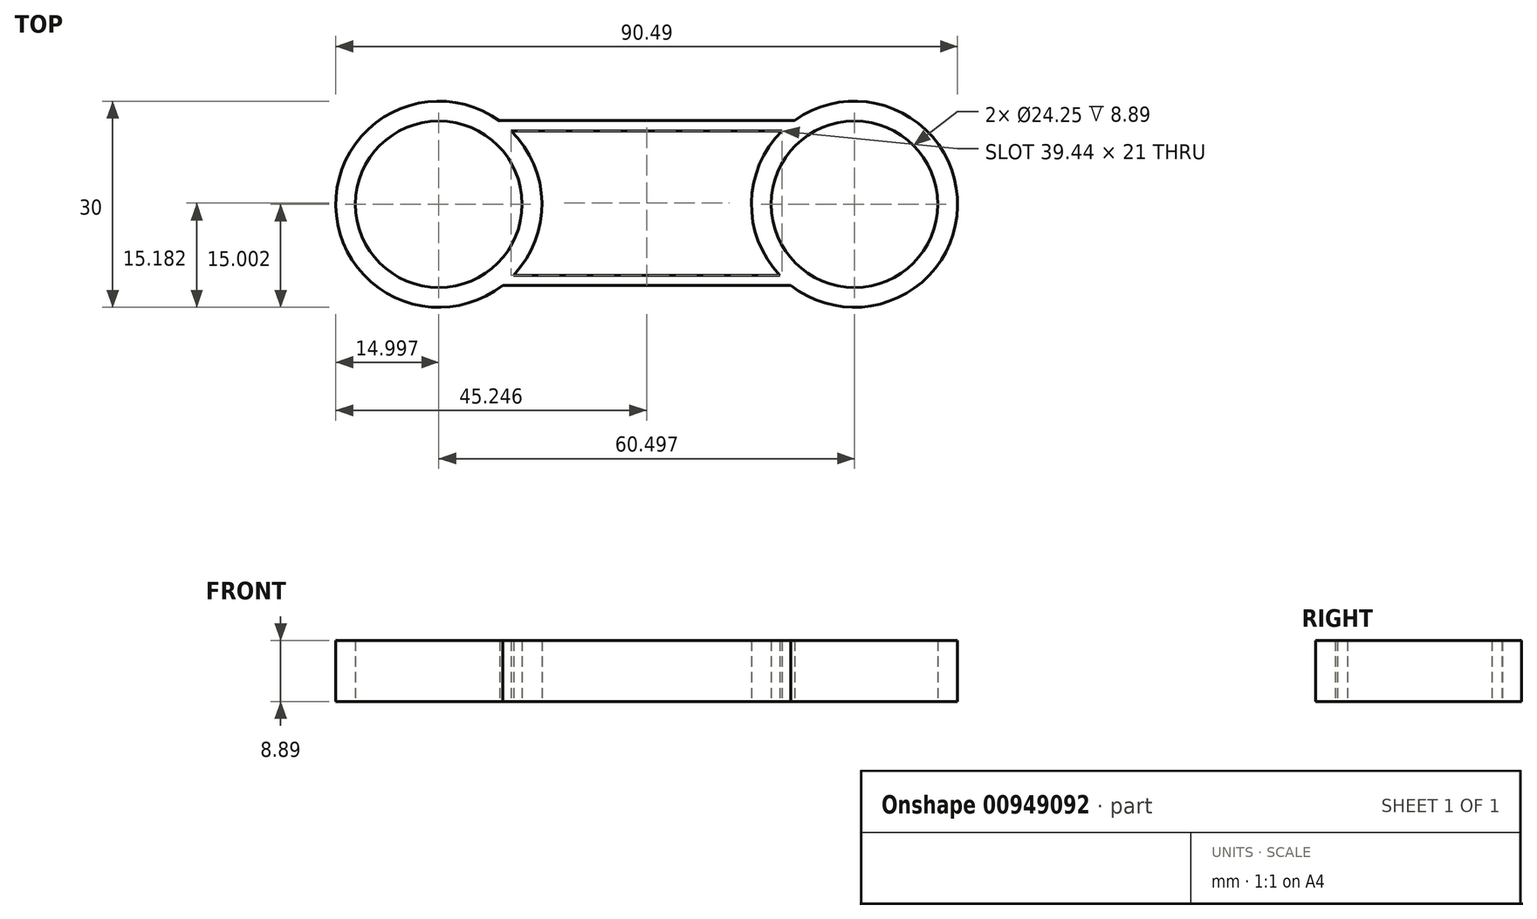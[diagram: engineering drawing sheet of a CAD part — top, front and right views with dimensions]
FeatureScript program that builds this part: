
annotation { "Feature Type Name" : "Feature", "Feature Type Description" : "" }
export const myFeature = defineFeature(function(context is Context, id is Id, definition is map)
    precondition{}
    {
        {
            var Q0;
            Q0=qCreatedBy(makeId("Top.planeOp"),FACE);
            var sketch = newSketch(context, id + "F0", { "sketchPlane" : qUnion([Q0])});
            skLineSegment(sketch, "E0.bottom", {"start": v(-19.42, -11.2) * mm, "end": v(23.58, -11.2) * mm});
            skLineSegment(sketch, "E0.top", {"start": v(-19.42, 12.8) * mm, "end": v(23.58, 12.8) * mm});
            skLineSegment(sketch, "E0.left", {"start": v(-19.42, -11.2) * mm, "end": v(-19.42, 12.8) * mm});
            skLineSegment(sketch, "E0.right", {"start": v(23.58, -11.2) * mm, "end": v(23.58, 12.8) * mm});
            skLineSegment(sketch, "E1.bottom", {"start": v(-18.21, -9.74) * mm, "end": v(22.29, -9.74) * mm});
            skLineSegment(sketch, "E1.top", {"start": v(-18.21, 11.26) * mm, "end": v(22.29, 11.26) * mm});
            skLineSegment(sketch, "E1.left", {"start": v(-18.21, -9.74) * mm, "end": v(-18.21, 11.26) * mm});
            skLineSegment(sketch, "E1.right", {"start": v(22.29, -9.74) * mm, "end": v(22.29, 11.26) * mm});
            skCircle(sketch, "E2", {"center": v(-28.27, 0.58) * mm, "radius": 12.12 * mm});
            skCircle(sketch, "E3", {"center": v(-28.27, 0.58) * mm, "radius": 15 * mm});
            skCircle(sketch, "E4", {"center": v(32.22, 0.58) * mm, "radius": 15 * mm});
            skCircle(sketch, "E5", {"center": v(32.22, 0.58) * mm, "radius": 12.12 * mm});
            skLineSegment(sketch, "E6.bottom", {"start": v(-43.27, -14.42) * mm, "end": v(47.22, -14.42) * mm});
            skLineSegment(sketch, "E6.top", {"start": v(-43.27, 15.58) * mm, "end": v(47.22, 15.58) * mm});
            skLineSegment(sketch, "E6.left", {"start": v(-43.27, -14.42) * mm, "end": v(-43.27, 15.58) * mm});
            skLineSegment(sketch, "E6.right", {"start": v(47.22, -14.42) * mm, "end": v(47.22, 15.58) * mm});
            skPoint(sketch, "E7", {"position": v(-32.27, -10.92) * mm});
            skSolve(sketch);
        }
        {
            var Q0;
            {var subQ1=sQuery(id+"F0.wireOp",EDGE,"E0.left");var subQ7=sQuery(id+"F0.wireOp",EDGE,"E0.bottom");var subQ8=makeQuery(id+"F0.imprint","INTERSECT",VERTEX,{"derivedFrom":[subQ7,subQ1]});Q0=makeQuery(id+"F0.imprint","IMPRINT",FACE,{"disambiguationData":[TD([[makeQuery(id+"F0.imprint","IMPRINT",EDGE,{"disambiguationData":[TD([[subQ8,-1.0]])],"derivedFrom":subQ7}),-1.0]])]});}
            var Q1;
            {var subQ0=sQuery(id+"F0.wireOp",EDGE,"E1.left");var subQ1=sQuery(id+"F0.wireOp",EDGE,"E1.bottom");var subQ2=makeQuery(id+"F0.imprint","INTERSECT",VERTEX,{"derivedFrom":[subQ1,subQ0]});Q1=makeQuery(id+"F0.imprint","IMPRINT",FACE,{"disambiguationData":[TD([[makeQuery(id+"F0.imprint","IMPRINT",EDGE,{"disambiguationData":[TD([[subQ2,-1.0]])],"derivedFrom":subQ1}),1.0]])]});}
            var Q2;
            {var subQ7=sQuery(id+"F0.wireOp",EDGE,"E0.left");var subQ8=sQuery(id+"F0.wireOp",EDGE,"E0.bottom");var subQ9=makeQuery(id+"F0.imprint","INTERSECT",VERTEX,{"derivedFrom":[subQ8,subQ7]});Q2=makeQuery(id+"F0.imprint","IMPRINT",FACE,{"disambiguationData":[TD([[makeQuery(id+"F0.imprint","IMPRINT",EDGE,{"disambiguationData":[TD([[subQ9,-1.0]])],"derivedFrom":subQ8}),1.0]])]});}
            var Q3;
            {var subQ0=sQuery(id+"F0.wireOp",EDGE,"E3");var subQ1=sQuery(id+"F0.wireOp",EDGE,"E0.bottom");var subQ2=makeQuery(id+"F0.imprint","INTERSECT",VERTEX,{"derivedFrom":[subQ1,subQ0]});Q3=makeQuery(id+"F0.imprint","IMPRINT",FACE,{"disambiguationData":[TD([[makeQuery(id+"F0.imprint","IMPRINT",EDGE,{"disambiguationData":[TD([[subQ2,-1.0]])],"derivedFrom":subQ1}),1.0]])]});}
            var Q4;
            {var subQ0=sQuery(id+"F0.wireOp",EDGE,"E2");var subQ1=sQuery(id+"F0.wireOp",EDGE,"E0.left");var subQ2=makeQuery(id+"F0.imprint","INTERSECT",VERTEX,{"disambiguationData":[OD(1.0)],"derivedFrom":[subQ1,subQ0]});Q4=makeQuery(id+"F0.imprint","IMPRINT",FACE,{"disambiguationData":[TD([[makeQuery(id+"F0.imprint","IMPRINT",EDGE,{"disambiguationData":[TD([[subQ2,-1.0]])],"derivedFrom":subQ1}),-1.0]])]});}
            var Q5;
            {var subQ5=sQuery(id+"F0.wireOp",EDGE,"E0.left");var subQ7=sQuery(id+"F0.wireOp",EDGE,"E0.top");var subQ8=makeQuery(id+"F0.imprint","INTERSECT",VERTEX,{"derivedFrom":[subQ7,subQ5]});Q5=makeQuery(id+"F0.imprint","IMPRINT",FACE,{"disambiguationData":[TD([[makeQuery(id+"F0.imprint","IMPRINT",EDGE,{"disambiguationData":[TD([[subQ8,-1.0]])],"derivedFrom":subQ7}),-1.0]])]});}
            var Q6;
            {var subQ7=sQuery(id+"F0.wireOp",EDGE,"E0.right");var subQ8=sQuery(id+"F0.wireOp",EDGE,"E0.top");var subQ9=makeQuery(id+"F0.imprint","INTERSECT",VERTEX,{"derivedFrom":[subQ8,subQ7]});Q6=makeQuery(id+"F0.imprint","IMPRINT",FACE,{"disambiguationData":[TD([[makeQuery(id+"F0.imprint","IMPRINT",EDGE,{"disambiguationData":[TD([[subQ9,1.0]])],"derivedFrom":subQ8}),-1.0]])]});}
            var Q7;
            {var subQ0=sQuery(id+"F0.wireOp",EDGE,"E0.right");var subQ5=sQuery(id+"F0.wireOp",EDGE,"E0.bottom");var subQ6=makeQuery(id+"F0.imprint","INTERSECT",VERTEX,{"derivedFrom":[subQ5,subQ0]});Q7=makeQuery(id+"F0.imprint","IMPRINT",FACE,{"disambiguationData":[TD([[makeQuery(id+"F0.imprint","IMPRINT",EDGE,{"disambiguationData":[TD([[subQ6,1.0]])],"derivedFrom":subQ5}),-1.0]])]});}
            var Q8;
            {var subQ7=sQuery(id+"F0.wireOp",EDGE,"E0.right");var subQ8=sQuery(id+"F0.wireOp",EDGE,"E0.bottom");var subQ9=makeQuery(id+"F0.imprint","INTERSECT",VERTEX,{"derivedFrom":[subQ8,subQ7]});Q8=makeQuery(id+"F0.imprint","IMPRINT",FACE,{"disambiguationData":[TD([[makeQuery(id+"F0.imprint","IMPRINT",EDGE,{"disambiguationData":[TD([[subQ9,1.0]])],"derivedFrom":subQ8}),1.0]])]});}
            var Q9;
            {var subQ0=sQuery(id+"F0.wireOp",EDGE,"E1.right");var subQ5=sQuery(id+"F0.wireOp",EDGE,"E1.bottom");var subQ6=makeQuery(id+"F0.imprint","INTERSECT",VERTEX,{"derivedFrom":[subQ5,subQ0]});Q9=makeQuery(id+"F0.imprint","IMPRINT",FACE,{"disambiguationData":[TD([[makeQuery(id+"F0.imprint","IMPRINT",EDGE,{"disambiguationData":[TD([[subQ6,1.0]])],"derivedFrom":subQ5}),1.0]])]});}
            extrude(context, id + "F1", {"entities" : qUnion([Q0, Q1, Q2, Q3, Q4, Q5, Q6, Q7, Q8, Q9]), "depth" : 8.9 * mm, "offsetDistance" : 25.4 * mm});
        }
    });
